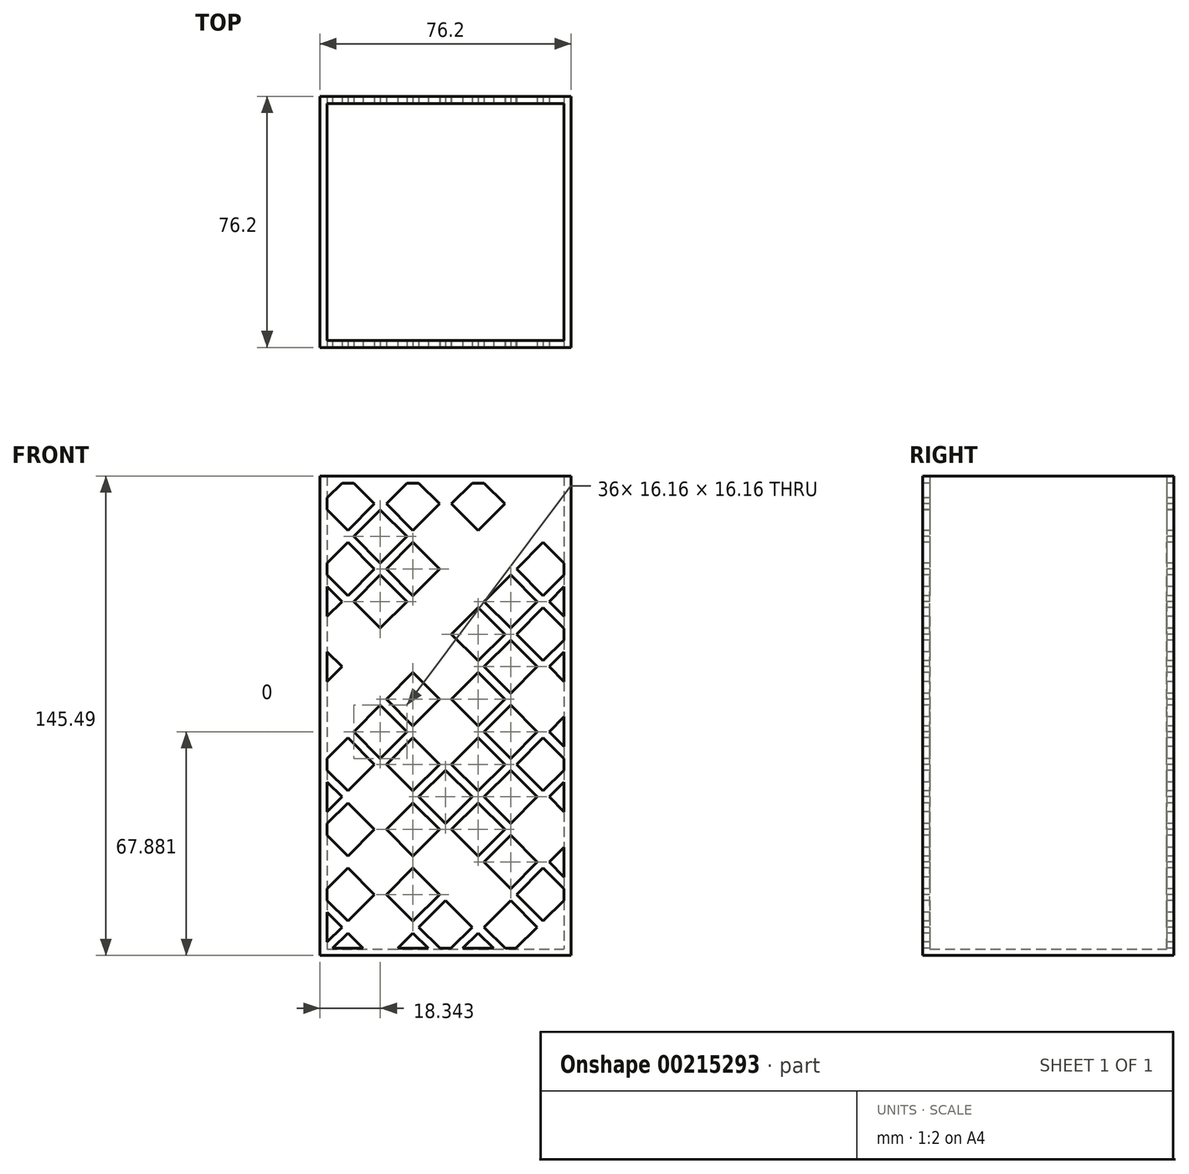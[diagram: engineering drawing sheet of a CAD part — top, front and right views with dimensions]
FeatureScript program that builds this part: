
annotation { "Feature Type Name" : "Feature", "Feature Type Description" : "" }
export const myFeature = defineFeature(function(context is Context, id is Id, definition is map)
    precondition{}
    {
        {
            var Q0;
            Q0=qCreatedBy(makeId("Top.planeOp"),FACE);
            var sketch = newSketch(context, id + "F0", { "sketchPlane" : qUnion([Q0])});
            skLineSegment(sketch, "E0.bottom", {"start": v(0, 0) * mm, "end": v(76.2, 0) * mm});
            skLineSegment(sketch, "E0.top", {"start": v(0, 76.2) * mm, "end": v(76.2, 76.2) * mm});
            skLineSegment(sketch, "E0.left", {"start": v(0, 0) * mm, "end": v(0, 76.2) * mm});
            skLineSegment(sketch, "E0.right", {"start": v(76.2, 0) * mm, "end": v(76.2, 76.2) * mm});
            skSolve(sketch);
        }
        {
            var Q0;
            Q0 = qSketchRegion(id + "F0", true);
            extrude(context, id + "F1", {"entities" : qUnion([Q0]), "depth" : 1.98 * mm});
        }
        {
            var Q0;
            Q0=makeQuery(id+"F1.opExtrude","CAP_FACE",FACE,{"disambiguationData":[OSD([sQuery(id+"F0.wireOp",EDGE,"E0.bottom"),sQuery(id+"F0.wireOp",EDGE,"E0.top"),sQuery(id+"F0.wireOp",EDGE,"E0.left"),sQuery(id+"F0.wireOp",EDGE,"E0.right")])],"isStart":false});
            var sketch = newSketch(context, id + "F2", { "sketchPlane" : qUnion([Q0])});
            skLineSegment(sketch, "E1.0", {"start": v(0, 76.2) * mm, "end": v(76.2, 76.2) * mm});
            skLineSegment(sketch, "E1.1", {"start": v(76.2, 0) * mm, "end": v(76.2, 76.2) * mm});
            skLineSegment(sketch, "E1.2", {"start": v(0, 0) * mm, "end": v(76.2, 0) * mm});
            skLineSegment(sketch, "E1.3", {"start": v(0, 0) * mm, "end": v(0, 76.2) * mm});
            skLineSegment(sketch, "E2.0", {"start": v(2.16, 2.16) * mm, "end": v(2.16, 74.04) * mm});
            skLineSegment(sketch, "E2.1", {"start": v(2.16, 2.16) * mm, "end": v(74.04, 2.16) * mm});
            skLineSegment(sketch, "E2.2", {"start": v(74.04, 2.16) * mm, "end": v(74.04, 74.04) * mm});
            skLineSegment(sketch, "E2.3", {"start": v(2.16, 74.04) * mm, "end": v(74.04, 74.04) * mm});
            skSolve(sketch);
        }
        {
            var Q0;
            Q0 = qSketchRegion(id + "F2", true);
            extrude(context, id + "F3", {"entities" : qUnion([Q0]), "operationType" : NewBodyOperationType.ADD, "depth" : 143.5 * mm});
        }
        {
            var Q0;
            Q0=makeQuery(id+"F3.boolean.opBoolean","MERGE",FACE,{"derivedFrom":[makeQuery(id+"F1.opExtrude","SWEPT_FACE",FACE,{"disambiguationData":[OSD([sQuery(id+"F0.wireOp",EDGE,"E0.bottom")])]}),makeQuery(id+"F3.opExtrude","SWEPT_FACE",FACE,{"disambiguationData":[OSD([sQuery(id+"F2.wireOp",EDGE,"E1.2")])]})]});
            var sketch = newSketch(context, id + "F4", { "sketchPlane" : qUnion([Q0])});
            skLineSegment(sketch, "E3", {"start": v(76.2, 137.41) * mm, "end": v(0, 61.21) * mm});
            skLineSegment(sketch, "E4", {"start": v(0, 61.21) * mm, "end": v(0, 77.38) * mm});
            skLineSegment(sketch, "E5", {"start": v(0, 77.38) * mm, "end": v(68.12, 145.5) * mm});
            skLineSegment(sketch, "E6", {"start": v(68.12, 145.5) * mm, "end": v(76.2, 145.5) * mm});
            skLineSegment(sketch, "E7", {"start": v(76.2, 145.5) * mm, "end": v(76.2, 137.41) * mm});
            skLineSegment(sketch, "E8", {"start": v(76.2, 133.82) * mm, "end": v(0, 57.62) * mm});
            skLineSegment(sketch, "E9", {"start": v(0, 57.62) * mm, "end": v(0, 41.46) * mm});
            skLineSegment(sketch, "E10", {"start": v(0, 41.46) * mm, "end": v(76.2, 117.66) * mm});
            skLineSegment(sketch, "E11", {"start": v(76.2, 117.66) * mm, "end": v(76.2, 133.82) * mm});
            skLineSegment(sketch, "E12", {"start": v(76.2, 114.06) * mm, "end": v(0, 37.86) * mm});
            skLineSegment(sketch, "E13", {"start": v(0, 37.86) * mm, "end": v(0, 21.7) * mm});
            skLineSegment(sketch, "E14", {"start": v(0, 21.7) * mm, "end": v(76.2, 97.9) * mm});
            skLineSegment(sketch, "E15", {"start": v(76.2, 97.9) * mm, "end": v(76.2, 114.06) * mm});
            skLineSegment(sketch, "E16", {"start": v(76.2, 94.3) * mm, "end": v(0, 18.1) * mm});
            skLineSegment(sketch, "E17", {"start": v(0, 18.1) * mm, "end": v(0, 1.94) * mm});
            skLineSegment(sketch, "E18", {"start": v(0, 1.94) * mm, "end": v(76.2, 78.14) * mm});
            skLineSegment(sketch, "E19", {"start": v(76.2, 78.14) * mm, "end": v(76.2, 94.3) * mm});
            skLineSegment(sketch, "E20", {"start": v(76.2, 74.55) * mm, "end": v(1.65, 0) * mm});
            skLineSegment(sketch, "E21", {"start": v(1.65, 0) * mm, "end": v(17.81, 0) * mm});
            skLineSegment(sketch, "E22", {"start": v(17.81, 0) * mm, "end": v(76.2, 58.39) * mm});
            skLineSegment(sketch, "E23", {"start": v(76.2, 58.39) * mm, "end": v(76.2, 74.55) * mm});
            skLineSegment(sketch, "E24", {"start": v(76.2, 54.8) * mm, "end": v(21.4, 0) * mm});
            skLineSegment(sketch, "E25", {"start": v(21.4, 0) * mm, "end": v(37.57, 0) * mm});
            skLineSegment(sketch, "E26", {"start": v(37.57, 0) * mm, "end": v(76.2, 38.63) * mm});
            skLineSegment(sketch, "E27", {"start": v(76.2, 38.63) * mm, "end": v(76.2, 54.8) * mm});
            skLineSegment(sketch, "E28", {"start": v(76.2, 35.04) * mm, "end": v(41.16, 0) * mm});
            skLineSegment(sketch, "E29", {"start": v(41.16, 0) * mm, "end": v(57.33, 0) * mm});
            skLineSegment(sketch, "E30", {"start": v(57.33, 0) * mm, "end": v(76.2, 18.87) * mm});
            skLineSegment(sketch, "E31", {"start": v(76.2, 18.87) * mm, "end": v(76.2, 35.04) * mm});
            skLineSegment(sketch, "E32", {"start": v(76.2, 15.28) * mm, "end": v(60.92, 0) * mm});
            skLineSegment(sketch, "E33", {"start": v(64.53, 145.5) * mm, "end": v(0, 80.97) * mm});
            skLineSegment(sketch, "E34", {"start": v(0, 80.97) * mm, "end": v(0, 97.13) * mm});
            skLineSegment(sketch, "E35", {"start": v(0, 97.13) * mm, "end": v(48.36, 145.5) * mm});
            skLineSegment(sketch, "E36", {"start": v(48.36, 145.5) * mm, "end": v(64.53, 145.5) * mm});
            skLineSegment(sketch, "E37", {"start": v(44.77, 145.5) * mm, "end": v(0, 100.72) * mm});
            skLineSegment(sketch, "E38", {"start": v(0, 100.72) * mm, "end": v(0, 116.89) * mm});
            skLineSegment(sketch, "E39", {"start": v(0, 116.89) * mm, "end": v(28.6, 145.5) * mm});
            skLineSegment(sketch, "E40", {"start": v(28.6, 145.5) * mm, "end": v(44.77, 145.5) * mm});
            skLineSegment(sketch, "E41", {"start": v(25.01, 145.5) * mm, "end": v(0, 120.48) * mm});
            skLineSegment(sketch, "E42", {"start": v(0, 120.48) * mm, "end": v(0, 136.65) * mm});
            skLineSegment(sketch, "E43", {"start": v(0, 136.65) * mm, "end": v(8.85, 145.5) * mm});
            skLineSegment(sketch, "E44", {"start": v(8.85, 145.5) * mm, "end": v(25.01, 145.5) * mm});
            skLineSegment(sketch, "E45", {"start": v(8.08, 145.5) * mm, "end": v(76.2, 77.38) * mm});
            skLineSegment(sketch, "E46", {"start": v(76.2, 77.38) * mm, "end": v(76.2, 61.21) * mm});
            skLineSegment(sketch, "E47", {"start": v(76.2, 61.21) * mm, "end": v(0, 137.41) * mm});
            skLineSegment(sketch, "E48", {"start": v(0, 133.82) * mm, "end": v(76.2, 57.62) * mm});
            skLineSegment(sketch, "E49", {"start": v(76.2, 57.62) * mm, "end": v(76.2, 41.46) * mm});
            skLineSegment(sketch, "E50", {"start": v(76.2, 41.46) * mm, "end": v(0, 117.66) * mm});
            skLineSegment(sketch, "E51", {"start": v(0, 117.66) * mm, "end": v(0, 133.82) * mm});
            skLineSegment(sketch, "E52", {"start": v(0, 114.06) * mm, "end": v(76.2, 37.86) * mm});
            skLineSegment(sketch, "E53", {"start": v(76.2, 37.86) * mm, "end": v(76.2, 21.7) * mm});
            skLineSegment(sketch, "E54", {"start": v(76.2, 21.7) * mm, "end": v(0, 97.9) * mm});
            skLineSegment(sketch, "E55", {"start": v(0, 97.9) * mm, "end": v(0, 114.06) * mm});
            skLineSegment(sketch, "E56", {"start": v(0, 94.3) * mm, "end": v(76.2, 18.1) * mm});
            skLineSegment(sketch, "E57", {"start": v(76.2, 18.1) * mm, "end": v(76.2, 15.28) * mm});
            skLineSegment(sketch, "E58", {"start": v(0, 78.14) * mm, "end": v(76.2, 1.94) * mm});
            skLineSegment(sketch, "E59", {"start": v(0, 74.55) * mm, "end": v(74.55, 0) * mm});
            skLineSegment(sketch, "E60", {"start": v(0, 58.39) * mm, "end": v(58.39, 0) * mm});
            skLineSegment(sketch, "E61", {"start": v(58.39, 0) * mm, "end": v(54.8, 0) * mm});
            skLineSegment(sketch, "E62", {"start": v(54.8, 0) * mm, "end": v(0, 54.8) * mm});
            skLineSegment(sketch, "E63", {"start": v(0, 54.8) * mm, "end": v(0, 58.39) * mm});
            skLineSegment(sketch, "E64", {"start": v(0, 38.63) * mm, "end": v(38.63, 0) * mm});
            skLineSegment(sketch, "E65", {"start": v(38.63, 0) * mm, "end": v(35.04, 0) * mm});
            skLineSegment(sketch, "E66", {"start": v(35.04, 0) * mm, "end": v(0, 35.04) * mm});
            skLineSegment(sketch, "E67", {"start": v(0, 35.04) * mm, "end": v(0, 38.63) * mm});
            skLineSegment(sketch, "E68", {"start": v(0, 18.87) * mm, "end": v(18.87, 0) * mm});
            skLineSegment(sketch, "E69", {"start": v(18.87, 0) * mm, "end": v(15.28, 0) * mm});
            skLineSegment(sketch, "E70", {"start": v(15.28, 0) * mm, "end": v(0, 15.28) * mm});
            skLineSegment(sketch, "E71", {"start": v(0, 15.28) * mm, "end": v(0, 18.87) * mm});
            skLineSegment(sketch, "E72", {"start": v(11.67, 145.5) * mm, "end": v(76.2, 80.97) * mm});
            skLineSegment(sketch, "E73", {"start": v(27.84, 145.5) * mm, "end": v(76.2, 97.13) * mm});
            skLineSegment(sketch, "E74", {"start": v(76.2, 97.13) * mm, "end": v(76.2, 100.72) * mm});
            skLineSegment(sketch, "E75", {"start": v(76.2, 100.72) * mm, "end": v(31.43, 145.5) * mm});
            skLineSegment(sketch, "E76", {"start": v(31.43, 145.5) * mm, "end": v(27.84, 145.5) * mm});
            skLineSegment(sketch, "E77", {"start": v(47.6, 145.5) * mm, "end": v(76.2, 116.89) * mm});
            skLineSegment(sketch, "E78", {"start": v(76.2, 116.89) * mm, "end": v(76.2, 120.48) * mm});
            skLineSegment(sketch, "E79", {"start": v(76.2, 120.48) * mm, "end": v(51.19, 145.5) * mm});
            skLineSegment(sketch, "E80", {"start": v(51.19, 145.5) * mm, "end": v(47.6, 145.5) * mm});
            skLineSegment(sketch, "E81", {"start": v(67.35, 145.5) * mm, "end": v(76.2, 136.65) * mm});
            skLineSegment(sketch, "E82.0", {"start": v(2.16, 2.16) * mm, "end": v(74.04, 2.16) * mm});
            skLineSegment(sketch, "E82.1", {"start": v(2.16, 143.34) * mm, "end": v(2.16, 2.16) * mm});
            skLineSegment(sketch, "E82.2", {"start": v(2.16, 143.34) * mm, "end": v(74.04, 143.34) * mm});
            skLineSegment(sketch, "E82.3", {"start": v(74.04, 143.34) * mm, "end": v(74.04, 2.16) * mm});
            skSolve(sketch);
        }
        {
            var Q0;
            {var subQ1=sQuery(id+"F4.wireOp",EDGE,"E41");var subQ5=sQuery(id+"F4.wireOp",EDGE,"E45");var subQ6=makeQuery(id+"F4.imprint","INTERSECT",VERTEX,{"derivedFrom":[subQ1,subQ5]});Q0=makeQuery(id+"F4.imprint","IMPRINT",FACE,{"disambiguationData":[TD([[makeQuery(id+"F4.imprint","IMPRINT",EDGE,{"disambiguationData":[TD([[subQ6,-1.0]])],"derivedFrom":subQ1}),-1.0]])]});}
            var Q1;
            {var subQ1=sQuery(id+"F4.wireOp",EDGE,"E37");var subQ5=sQuery(id+"F4.wireOp",EDGE,"E73");var subQ6=makeQuery(id+"F4.imprint","INTERSECT",VERTEX,{"derivedFrom":[subQ1,subQ5]});Q1=makeQuery(id+"F4.imprint","IMPRINT",FACE,{"disambiguationData":[TD([[makeQuery(id+"F4.imprint","IMPRINT",EDGE,{"disambiguationData":[TD([[subQ6,-1.0]])],"derivedFrom":subQ1}),-1.0]])]});}
            var Q2;
            {var subQ0=sQuery(id+"F4.wireOp",EDGE,"E77");var subQ1=sQuery(id+"F4.wireOp",EDGE,"E33");var subQ2=makeQuery(id+"F4.imprint","INTERSECT",VERTEX,{"derivedFrom":[subQ1,subQ0]});Q2=makeQuery(id+"F4.imprint","IMPRINT",FACE,{"disambiguationData":[TD([[makeQuery(id+"F4.imprint","IMPRINT",EDGE,{"disambiguationData":[TD([[subQ2,-1.0]])],"derivedFrom":subQ1}),-1.0]])]});}
            var Q3;
            {var subQ0=sQuery(id+"F4.wireOp",EDGE,"E45");var subQ1=sQuery(id+"F4.wireOp",EDGE,"E37");var subQ2=makeQuery(id+"F4.imprint","INTERSECT",VERTEX,{"derivedFrom":[subQ1,subQ0]});Q3=makeQuery(id+"F4.imprint","IMPRINT",FACE,{"disambiguationData":[TD([[makeQuery(id+"F4.imprint","IMPRINT",EDGE,{"disambiguationData":[TD([[subQ2,-1.0]])],"derivedFrom":subQ1}),-1.0]])]});}
            var Q4;
            {var subQ1=sQuery(id+"F4.wireOp",EDGE,"E37");var subQ5=sQuery(id+"F4.wireOp",EDGE,"E48");var subQ6=makeQuery(id+"F4.imprint","INTERSECT",VERTEX,{"derivedFrom":[subQ1,subQ5]});Q4=makeQuery(id+"F4.imprint","IMPRINT",FACE,{"disambiguationData":[TD([[makeQuery(id+"F4.imprint","IMPRINT",EDGE,{"disambiguationData":[TD([[subQ6,-1.0]])],"derivedFrom":subQ1}),-1.0]])]});}
            var Q5;
            {var subQ0=sQuery(id+"F4.wireOp",EDGE,"E48");var subQ1=sQuery(id+"F4.wireOp",EDGE,"E33");var subQ2=makeQuery(id+"F4.imprint","INTERSECT",VERTEX,{"derivedFrom":[subQ1,subQ0]});Q5=makeQuery(id+"F4.imprint","IMPRINT",FACE,{"disambiguationData":[TD([[makeQuery(id+"F4.imprint","IMPRINT",EDGE,{"disambiguationData":[TD([[subQ2,-1.0]])],"derivedFrom":subQ1}),-1.0]])]});}
            var Q6;
            {var subQ0=sQuery(id+"F4.wireOp",EDGE,"E45");var subQ1=sQuery(id+"F4.wireOp",EDGE,"E33");var subQ2=makeQuery(id+"F4.imprint","INTERSECT",VERTEX,{"derivedFrom":[subQ1,subQ0]});Q6=makeQuery(id+"F4.imprint","IMPRINT",FACE,{"disambiguationData":[TD([[makeQuery(id+"F4.imprint","IMPRINT",EDGE,{"disambiguationData":[TD([[subQ2,-1.0]])],"derivedFrom":subQ1}),-1.0]])]});}
            var Q7;
            {var subQ1=sQuery(id+"F4.wireOp",EDGE,"E8");var subQ7=sQuery(id+"F4.wireOp",EDGE,"E77");var subQ8=makeQuery(id+"F4.imprint","INTERSECT",VERTEX,{"derivedFrom":[subQ1,subQ7]});Q7=makeQuery(id+"F4.imprint","IMPRINT",FACE,{"disambiguationData":[TD([[makeQuery(id+"F4.imprint","IMPRINT",EDGE,{"disambiguationData":[TD([[subQ8,-1.0]])],"derivedFrom":subQ1}),1.0]])]});}
            var Q8;
            {var subQ0=sQuery(id+"F4.wireOp",EDGE,"E73");var subQ1=sQuery(id+"F4.wireOp",EDGE,"E8");var subQ2=makeQuery(id+"F4.imprint","INTERSECT",VERTEX,{"derivedFrom":[subQ1,subQ0]});Q8=makeQuery(id+"F4.imprint","IMPRINT",FACE,{"disambiguationData":[TD([[makeQuery(id+"F4.imprint","IMPRINT",EDGE,{"disambiguationData":[TD([[subQ2,-1.0]])],"derivedFrom":subQ1}),1.0]])]});}
            var Q9;
            {var subQ0=sQuery(id+"F4.wireOp",EDGE,"E45");var subQ1=sQuery(id+"F4.wireOp",EDGE,"E8");var subQ2=makeQuery(id+"F4.imprint","INTERSECT",VERTEX,{"derivedFrom":[subQ1,subQ0]});Q9=makeQuery(id+"F4.imprint","IMPRINT",FACE,{"disambiguationData":[TD([[makeQuery(id+"F4.imprint","IMPRINT",EDGE,{"disambiguationData":[TD([[subQ2,-1.0]])],"derivedFrom":subQ1}),1.0]])]});}
            var Q10;
            {var subQ0=sQuery(id+"F4.wireOp",EDGE,"E52");var subQ1=sQuery(id+"F4.wireOp",EDGE,"E8");var subQ2=makeQuery(id+"F4.imprint","INTERSECT",VERTEX,{"derivedFrom":[subQ1,subQ0]});Q10=makeQuery(id+"F4.imprint","IMPRINT",FACE,{"disambiguationData":[TD([[makeQuery(id+"F4.imprint","IMPRINT",EDGE,{"disambiguationData":[TD([[subQ2,-1.0]])],"derivedFrom":subQ1}),1.0]])]});}
            var Q11;
            {var subQ0=sQuery(id+"F4.wireOp",EDGE,"E56");var subQ1=sQuery(id+"F4.wireOp",EDGE,"E8");var subQ2=makeQuery(id+"F4.imprint","INTERSECT",VERTEX,{"derivedFrom":[subQ1,subQ0]});Q11=makeQuery(id+"F4.imprint","IMPRINT",FACE,{"disambiguationData":[TD([[makeQuery(id+"F4.imprint","IMPRINT",EDGE,{"disambiguationData":[TD([[subQ2,-1.0]])],"derivedFrom":subQ1}),1.0]])]});}
            var Q12;
            {var subQ5=sQuery(id+"F4.wireOp",EDGE,"E59");var subQ6=sQuery(id+"F4.wireOp",EDGE,"E8");var subQ7=makeQuery(id+"F4.imprint","INTERSECT",VERTEX,{"derivedFrom":[subQ6,subQ5]});Q12=makeQuery(id+"F4.imprint","IMPRINT",FACE,{"disambiguationData":[TD([[makeQuery(id+"F4.imprint","IMPRINT",EDGE,{"disambiguationData":[TD([[subQ7,-1.0]])],"derivedFrom":subQ6}),1.0]])]});}
            var Q13;
            {var subQ0=sQuery(id+"F4.wireOp",EDGE,"E73");var subQ1=sQuery(id+"F4.wireOp",EDGE,"E12");var subQ2=makeQuery(id+"F4.imprint","INTERSECT",VERTEX,{"derivedFrom":[subQ1,subQ0]});Q13=makeQuery(id+"F4.imprint","IMPRINT",FACE,{"disambiguationData":[TD([[makeQuery(id+"F4.imprint","IMPRINT",EDGE,{"disambiguationData":[TD([[subQ2,-1.0]])],"derivedFrom":subQ1}),1.0]])]});}
            var Q14;
            {var subQ0=sQuery(id+"F4.wireOp",EDGE,"E45");var subQ1=sQuery(id+"F4.wireOp",EDGE,"E12");var subQ2=makeQuery(id+"F4.imprint","INTERSECT",VERTEX,{"derivedFrom":[subQ1,subQ0]});Q14=makeQuery(id+"F4.imprint","IMPRINT",FACE,{"disambiguationData":[TD([[makeQuery(id+"F4.imprint","IMPRINT",EDGE,{"disambiguationData":[TD([[subQ2,-1.0]])],"derivedFrom":subQ1}),1.0]])]});}
            var Q15;
            {var subQ0=sQuery(id+"F4.wireOp",EDGE,"E48");var subQ1=sQuery(id+"F4.wireOp",EDGE,"E12");var subQ2=makeQuery(id+"F4.imprint","INTERSECT",VERTEX,{"derivedFrom":[subQ1,subQ0]});Q15=makeQuery(id+"F4.imprint","IMPRINT",FACE,{"disambiguationData":[TD([[makeQuery(id+"F4.imprint","IMPRINT",EDGE,{"disambiguationData":[TD([[subQ2,-1.0]])],"derivedFrom":subQ1}),1.0]])]});}
            var Q16;
            {var subQ0=sQuery(id+"F4.wireOp",EDGE,"E56");var subQ1=sQuery(id+"F4.wireOp",EDGE,"E12");var subQ2=makeQuery(id+"F4.imprint","INTERSECT",VERTEX,{"derivedFrom":[subQ1,subQ0]});Q16=makeQuery(id+"F4.imprint","IMPRINT",FACE,{"disambiguationData":[TD([[makeQuery(id+"F4.imprint","IMPRINT",EDGE,{"disambiguationData":[TD([[subQ2,-1.0]])],"derivedFrom":subQ1}),1.0]])]});}
            var Q17;
            {var subQ5=sQuery(id+"F4.wireOp",EDGE,"E62");var subQ6=sQuery(id+"F4.wireOp",EDGE,"E12");var subQ7=makeQuery(id+"F4.imprint","INTERSECT",VERTEX,{"derivedFrom":[subQ6,subQ5]});Q17=makeQuery(id+"F4.imprint","IMPRINT",FACE,{"disambiguationData":[TD([[makeQuery(id+"F4.imprint","IMPRINT",EDGE,{"disambiguationData":[TD([[subQ7,-1.0]])],"derivedFrom":subQ6}),1.0]])]});}
            var Q18;
            {var subQ0=sQuery(id+"F4.wireOp",EDGE,"E48");var subQ1=sQuery(id+"F4.wireOp",EDGE,"E16");var subQ2=makeQuery(id+"F4.imprint","INTERSECT",VERTEX,{"derivedFrom":[subQ1,subQ0]});Q18=makeQuery(id+"F4.imprint","IMPRINT",FACE,{"disambiguationData":[TD([[makeQuery(id+"F4.imprint","IMPRINT",EDGE,{"disambiguationData":[TD([[subQ2,-1.0]])],"derivedFrom":subQ1}),1.0]])]});}
            var Q19;
            {var subQ0=sQuery(id+"F4.wireOp",EDGE,"E52");var subQ1=sQuery(id+"F4.wireOp",EDGE,"E16");var subQ2=makeQuery(id+"F4.imprint","INTERSECT",VERTEX,{"derivedFrom":[subQ1,subQ0]});Q19=makeQuery(id+"F4.imprint","IMPRINT",FACE,{"disambiguationData":[TD([[makeQuery(id+"F4.imprint","IMPRINT",EDGE,{"disambiguationData":[TD([[subQ2,-1.0]])],"derivedFrom":subQ1}),1.0]])]});}
            var Q20;
            {var subQ0=sQuery(id+"F4.wireOp",EDGE,"E56");var subQ1=sQuery(id+"F4.wireOp",EDGE,"E16");var subQ2=makeQuery(id+"F4.imprint","INTERSECT",VERTEX,{"derivedFrom":[subQ1,subQ0]});Q20=makeQuery(id+"F4.imprint","IMPRINT",FACE,{"disambiguationData":[TD([[makeQuery(id+"F4.imprint","IMPRINT",EDGE,{"disambiguationData":[TD([[subQ2,-1.0]])],"derivedFrom":subQ1}),1.0]])]});}
            var Q21;
            {var subQ0=sQuery(id+"F4.wireOp",EDGE,"E59");var subQ1=sQuery(id+"F4.wireOp",EDGE,"E16");var subQ2=makeQuery(id+"F4.imprint","INTERSECT",VERTEX,{"derivedFrom":[subQ1,subQ0]});Q21=makeQuery(id+"F4.imprint","IMPRINT",FACE,{"disambiguationData":[TD([[makeQuery(id+"F4.imprint","IMPRINT",EDGE,{"disambiguationData":[TD([[subQ2,-1.0]])],"derivedFrom":subQ1}),1.0]])]});}
            var Q22;
            {var subQ0=sQuery(id+"F4.wireOp",EDGE,"E66");var subQ1=sQuery(id+"F4.wireOp",EDGE,"E16");var subQ2=makeQuery(id+"F4.imprint","INTERSECT",VERTEX,{"derivedFrom":[subQ1,subQ0]});Q22=makeQuery(id+"F4.imprint","IMPRINT",FACE,{"disambiguationData":[TD([[makeQuery(id+"F4.imprint","IMPRINT",EDGE,{"disambiguationData":[TD([[subQ2,-1.0]])],"derivedFrom":subQ1}),1.0]])]});}
            var Q23;
            {var subQ1=sQuery(id+"F4.wireOp",EDGE,"E20");var subQ5=sQuery(id+"F4.wireOp",EDGE,"E48");var subQ6=makeQuery(id+"F4.imprint","INTERSECT",VERTEX,{"derivedFrom":[subQ1,subQ5]});Q23=makeQuery(id+"F4.imprint","IMPRINT",FACE,{"disambiguationData":[TD([[makeQuery(id+"F4.imprint","IMPRINT",EDGE,{"disambiguationData":[TD([[subQ6,-1.0]])],"derivedFrom":subQ1}),1.0]])]});}
            var Q24;
            {var subQ0=sQuery(id+"F4.wireOp",EDGE,"E52");var subQ1=sQuery(id+"F4.wireOp",EDGE,"E20");var subQ2=makeQuery(id+"F4.imprint","INTERSECT",VERTEX,{"derivedFrom":[subQ1,subQ0]});Q24=makeQuery(id+"F4.imprint","IMPRINT",FACE,{"disambiguationData":[TD([[makeQuery(id+"F4.imprint","IMPRINT",EDGE,{"disambiguationData":[TD([[subQ2,-1.0]])],"derivedFrom":subQ1}),1.0]])]});}
            var Q25;
            {var subQ0=sQuery(id+"F4.wireOp",EDGE,"E56");var subQ1=sQuery(id+"F4.wireOp",EDGE,"E20");var subQ2=makeQuery(id+"F4.imprint","INTERSECT",VERTEX,{"derivedFrom":[subQ1,subQ0]});Q25=makeQuery(id+"F4.imprint","IMPRINT",FACE,{"disambiguationData":[TD([[makeQuery(id+"F4.imprint","IMPRINT",EDGE,{"disambiguationData":[TD([[subQ2,-1.0]])],"derivedFrom":subQ1}),1.0]])]});}
            var Q26;
            {var subQ0=sQuery(id+"F4.wireOp",EDGE,"E52");var subQ1=sQuery(id+"F4.wireOp",EDGE,"E37");var subQ2=makeQuery(id+"F4.imprint","INTERSECT",VERTEX,{"derivedFrom":[subQ1,subQ0]});Q26=makeQuery(id+"F4.imprint","IMPRINT",FACE,{"disambiguationData":[TD([[makeQuery(id+"F4.imprint","IMPRINT",EDGE,{"disambiguationData":[TD([[subQ2,-1.0]])],"derivedFrom":subQ1}),-1.0]])]});}
            var Q27;
            {var subQ0=sQuery(id+"F4.wireOp",EDGE,"E82.3");var subQ1=sQuery(id+"F4.wireOp",EDGE,"E12");var subQ2=makeQuery(id+"F4.imprint","INTERSECT",VERTEX,{"derivedFrom":[subQ1,subQ0]});Q27=makeQuery(id+"F4.imprint","IMPRINT",FACE,{"disambiguationData":[TD([[makeQuery(id+"F4.imprint","IMPRINT",EDGE,{"disambiguationData":[TD([[subQ2,-1.0]])],"derivedFrom":subQ1}),1.0]])]});}
            var Q28;
            {var subQ0=sQuery(id+"F4.wireOp",EDGE,"E82.3");var subQ1=sQuery(id+"F4.wireOp",EDGE,"E16");var subQ2=makeQuery(id+"F4.imprint","INTERSECT",VERTEX,{"derivedFrom":[subQ1,subQ0]});Q28=makeQuery(id+"F4.imprint","IMPRINT",FACE,{"disambiguationData":[TD([[makeQuery(id+"F4.imprint","IMPRINT",EDGE,{"disambiguationData":[TD([[subQ2,-1.0]])],"derivedFrom":subQ1}),1.0]])]});}
            var Q29;
            {var subQ0=sQuery(id+"F4.wireOp",EDGE,"E82.3");var subQ1=sQuery(id+"F4.wireOp",EDGE,"E20");var subQ2=makeQuery(id+"F4.imprint","INTERSECT",VERTEX,{"derivedFrom":[subQ1,subQ0]});Q29=makeQuery(id+"F4.imprint","IMPRINT",FACE,{"disambiguationData":[TD([[makeQuery(id+"F4.imprint","IMPRINT",EDGE,{"disambiguationData":[TD([[subQ2,-1.0]])],"derivedFrom":subQ1}),1.0]])]});}
            var Q30;
            {var subQ0=sQuery(id+"F4.wireOp",EDGE,"E82.1");var subQ1=sQuery(id+"F4.wireOp",EDGE,"E10");var subQ2=makeQuery(id+"F4.imprint","INTERSECT",VERTEX,{"derivedFrom":[subQ1,subQ0]});Q30=makeQuery(id+"F4.imprint","IMPRINT",FACE,{"disambiguationData":[TD([[makeQuery(id+"F4.imprint","IMPRINT",EDGE,{"disambiguationData":[TD([[subQ2,-1.0]])],"derivedFrom":subQ1}),1.0]])]});}
            var Q31;
            {var subQ0=sQuery(id+"F4.wireOp",EDGE,"E62");var subQ1=sQuery(id+"F4.wireOp",EDGE,"E20");var subQ2=makeQuery(id+"F4.imprint","INTERSECT",VERTEX,{"derivedFrom":[subQ1,subQ0]});Q31=makeQuery(id+"F4.imprint","IMPRINT",FACE,{"disambiguationData":[TD([[makeQuery(id+"F4.imprint","IMPRINT",EDGE,{"disambiguationData":[TD([[subQ2,-1.0]])],"derivedFrom":subQ1}),1.0]])]});}
            var Q32;
            {var subQ0=sQuery(id+"F4.wireOp",EDGE,"E82.3");var subQ1=sQuery(id+"F4.wireOp",EDGE,"E24");var subQ2=makeQuery(id+"F4.imprint","INTERSECT",VERTEX,{"derivedFrom":[subQ1,subQ0]});Q32=makeQuery(id+"F4.imprint","IMPRINT",FACE,{"disambiguationData":[TD([[makeQuery(id+"F4.imprint","IMPRINT",EDGE,{"disambiguationData":[TD([[subQ2,-1.0]])],"derivedFrom":subQ1}),1.0]])]});}
            var Q33;
            {var subQ0=sQuery(id+"F4.wireOp",EDGE,"E82.3");var subQ1=sQuery(id+"F4.wireOp",EDGE,"E28");var subQ2=makeQuery(id+"F4.imprint","INTERSECT",VERTEX,{"derivedFrom":[subQ1,subQ0]});Q33=makeQuery(id+"F4.imprint","IMPRINT",FACE,{"disambiguationData":[TD([[makeQuery(id+"F4.imprint","IMPRINT",EDGE,{"disambiguationData":[TD([[subQ2,-1.0]])],"derivedFrom":subQ1}),1.0]])]});}
            var Q34;
            {var subQ0=sQuery(id+"F4.wireOp",EDGE,"E56");var subQ1=sQuery(id+"F4.wireOp",EDGE,"E24");var subQ2=makeQuery(id+"F4.imprint","INTERSECT",VERTEX,{"derivedFrom":[subQ1,subQ0]});Q34=makeQuery(id+"F4.imprint","IMPRINT",FACE,{"disambiguationData":[TD([[makeQuery(id+"F4.imprint","IMPRINT",EDGE,{"disambiguationData":[TD([[subQ2,-1.0]])],"derivedFrom":subQ1}),1.0]])]});}
            var Q35;
            {var subQ0=sQuery(id+"F4.wireOp",EDGE,"E70");var subQ1=sQuery(id+"F4.wireOp",EDGE,"E20");var subQ2=makeQuery(id+"F4.imprint","INTERSECT",VERTEX,{"derivedFrom":[subQ1,subQ0]});Q35=makeQuery(id+"F4.imprint","IMPRINT",FACE,{"disambiguationData":[TD([[makeQuery(id+"F4.imprint","IMPRINT",EDGE,{"disambiguationData":[TD([[subQ2,-1.0]])],"derivedFrom":subQ1}),1.0]])]});}
            var Q36;
            {var subQ0=sQuery(id+"F4.wireOp",EDGE,"E62");var subQ1=sQuery(id+"F4.wireOp",EDGE,"E28");var subQ2=makeQuery(id+"F4.imprint","INTERSECT",VERTEX,{"derivedFrom":[subQ1,subQ0]});Q36=makeQuery(id+"F4.imprint","IMPRINT",FACE,{"disambiguationData":[TD([[makeQuery(id+"F4.imprint","IMPRINT",EDGE,{"disambiguationData":[TD([[subQ2,-1.0]])],"derivedFrom":subQ1}),1.0]])]});}
            var Q37;
            {var subQ1=sQuery(id+"F4.wireOp",EDGE,"E28");var subQ7=sQuery(id+"F4.wireOp",EDGE,"E59");var subQ9=makeQuery(id+"F4.imprint","INTERSECT",VERTEX,{"derivedFrom":[subQ1,subQ7]});Q37=makeQuery(id+"F4.imprint","IMPRINT",FACE,{"disambiguationData":[TD([[makeQuery(id+"F4.imprint","IMPRINT",EDGE,{"disambiguationData":[TD([[subQ9,-1.0]])],"derivedFrom":subQ1}),1.0]])]});}
            var Q38;
            {var subQ0=sQuery(id+"F4.wireOp",EDGE,"E66");var subQ1=sQuery(id+"F4.wireOp",EDGE,"E24");var subQ2=makeQuery(id+"F4.imprint","INTERSECT",VERTEX,{"derivedFrom":[subQ1,subQ0]});Q38=makeQuery(id+"F4.imprint","IMPRINT",FACE,{"disambiguationData":[TD([[makeQuery(id+"F4.imprint","IMPRINT",EDGE,{"disambiguationData":[TD([[subQ2,-1.0]])],"derivedFrom":subQ1}),1.0]])]});}
            var Q39;
            {var subQ0=sQuery(id+"F4.wireOp",EDGE,"E56");var subQ1=sQuery(id+"F4.wireOp",EDGE,"E33");var subQ2=makeQuery(id+"F4.imprint","INTERSECT",VERTEX,{"derivedFrom":[subQ1,subQ0]});Q39=makeQuery(id+"F4.imprint","IMPRINT",FACE,{"disambiguationData":[TD([[makeQuery(id+"F4.imprint","IMPRINT",EDGE,{"disambiguationData":[TD([[subQ2,-1.0]])],"derivedFrom":subQ1}),-1.0]])]});}
            var Q40;
            {var subQ0=sQuery(id+"F4.wireOp",EDGE,"E82.1");var subQ1=sQuery(id+"F4.wireOp",EDGE,"E18");var subQ2=makeQuery(id+"F4.imprint","INTERSECT",VERTEX,{"derivedFrom":[subQ1,subQ0]});Q40=makeQuery(id+"F4.imprint","IMPRINT",FACE,{"disambiguationData":[TD([[makeQuery(id+"F4.imprint","IMPRINT",EDGE,{"disambiguationData":[TD([[subQ2,-1.0]])],"derivedFrom":subQ1}),1.0]])]});}
            var Q41;
            {var subQ1=sQuery(id+"F4.wireOp",EDGE,"E24");var subQ7=sQuery(id+"F4.wireOp",EDGE,"E62");var subQ9=makeQuery(id+"F4.imprint","INTERSECT",VERTEX,{"derivedFrom":[subQ1,subQ7]});Q41=makeQuery(id+"F4.imprint","IMPRINT",FACE,{"disambiguationData":[TD([[makeQuery(id+"F4.imprint","IMPRINT",EDGE,{"disambiguationData":[TD([[subQ9,-1.0]])],"derivedFrom":subQ1}),1.0]])]});}
            var Q42;
            {var subQ1=sQuery(id+"F4.wireOp",EDGE,"E28");var subQ5=sQuery(id+"F4.wireOp",EDGE,"E56");var subQ6=makeQuery(id+"F4.imprint","INTERSECT",VERTEX,{"derivedFrom":[subQ1,subQ5]});Q42=makeQuery(id+"F4.imprint","IMPRINT",FACE,{"disambiguationData":[TD([[makeQuery(id+"F4.imprint","IMPRINT",EDGE,{"disambiguationData":[TD([[subQ6,-1.0]])],"derivedFrom":subQ1}),1.0]])]});}
            extrude(context, id + "F5", {"entities" : qUnion([Q0, Q1, Q2, Q3, Q4, Q5, Q6, Q7, Q8, Q9, Q10, Q11, Q12, Q13, Q14, Q15, Q16, Q17, Q18, Q19, Q20, Q21, Q22, Q23, Q24, Q25, Q26, Q27, Q28, Q29, Q30, Q31, Q32, Q33, Q34, Q35, Q36, Q37, Q38, Q39, Q40, Q41, Q42]), "operationType" : NewBodyOperationType.REMOVE, "endBound" : BoundingType.THROUGH_ALL, "oppositeDirection" : true, "depth" : 25.4 * mm});
        }
    });
